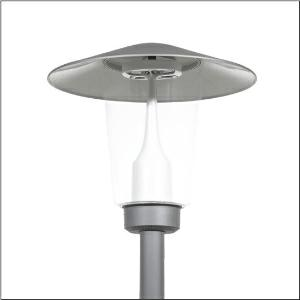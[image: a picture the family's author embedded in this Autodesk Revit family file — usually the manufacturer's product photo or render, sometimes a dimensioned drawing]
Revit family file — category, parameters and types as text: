
# Revit family: pilzleuchte_iq___p1_0a_5xa5235nf14hp_8191
name_source: partatom
category: Lighting Fixtures
units: mm (PartAtom-declared; Revit-internal decimal feet)

## family parameters
Cut with Voids When Loaded = No
Host = Face
Light Source = No
Part Type = Normal
Room Calculation Point = No
Round Connector Dimension = Use Diameter
Shared = No

## types (1)
- --- (1 x LED, 4250 lm, 33.6 W, 2700K)
    Apparent Load = 34 VA
    CIE Flux Codes = 35 64 90 96 100
    Color Rendering = 70
    Color Temperature = 2700K
    Default Elevation = 1800 mm
    Description = Mushroom Luminaire iQ, mast luminaire, Module 540 iQ-SR, primary light control with 3 zone facetted reflector, of plastic, silver coated, highly specular, structured, primary optical cover: cover, of PMMA, transparent, light distribution: P1.0a, light emission: direct distribution, primary light characteristic: strongly asymmetric, installation type: post-top, LED, High Power LED, rated luminous flux: 4.250lm, luminous efficacy: 127lm/W, light colour: 727, colour temperature: 2700K, control gear: ECG iQ, control: pre-setting: logarithmic dimming characteristic, Street-Remote, Auto-Match, Temp-Guard, Lumen-Switch, Night-Set, Smart-Wire, Light-Fading, Desk-Remote (wireless, voltage-free reading and setting of iQ features in the workshop via application-optimized NFC function/RFID function), optimised constant luminous flux control (CLO 2.0), with terminal, 6-pole, max. 2.5mm², mains connection: 230..240V, AC, 50/60Hz, start of lifetime: 34W, end of service life: 36W, reduction: 15W, luminaire housing, upper part, of glass-fibre reinforced polyester, coated, Siteco® metallic grey (DB 702S), diameter: 650mm, height: 586mm, spigot size: d x l = 76 x 70mm (post-top) | with reducer (optional accessory) 60 x 70mm, post-top mast mounting element, of diecast aluminium, coated, Siteco® metallic grey (DB 702S), Module 540 iQ-SR, traffic white (RAL 9016), equipment: Power, protection rating (complete): IP65, insulation class (complete): insulation class II (safety insulation), certification: CE, ENEC, VDE, packaging unit: 1 piece

Light Distribution: P1.0a
    Height = 586 mm
    Lamp = 1 x LED
    Lamp Light Flux = 4250 lm
    Lamp Power = 33.6 W
    Lamp count = 1
    Length = 650 mm
    Luminous efficacy = 126 lm/W
    Manufacturer = Siteco
    ModVariant = No
    Model = 5XA5235NF14HP
    Number of Poles = 1
    OnlyDefault = Yes
    Power Factor = 1
    Product Name = Pilzleuchte iQ | P1.0a
    Product group = mast luminaire | pylon top
    ProductGroupID = 6100
    Protection Class = Protection class II
    Protection Degree = IP 65
    RLX_Detail_Level = 1
    RLX_Emergency_Light_Flux = 0 lm
    RLX_Emergency_Type = 0
    RLX_Emergency_Type_DB = No
    RlxData = <blob elided: 52101 chars, md5=ad3eff07>
    Socket = socket
    Standby Power = 0 W
    System Light Flux = 4250 lm
    System Power = 34 W
    Type Comments = factory setting: luminous flux: 100 % | dim-lin: 254 | 695 mA
    Type Image = l_1006077.jpg
    URL = http://relux.com
    VarID = @adj_122659
    Voltage = 0 V
    Weight = 0.00 kg
    Width = 0 mm  [stored 0 ft]

note: [stored X ft] marks values corroborated as IEEE doubles in the binary element streams (Revit-internal decimal feet)

## geometry (parser evidence)
native form markers: Blend x4, Sweep x13
no freeform markers — native parametric forms only
